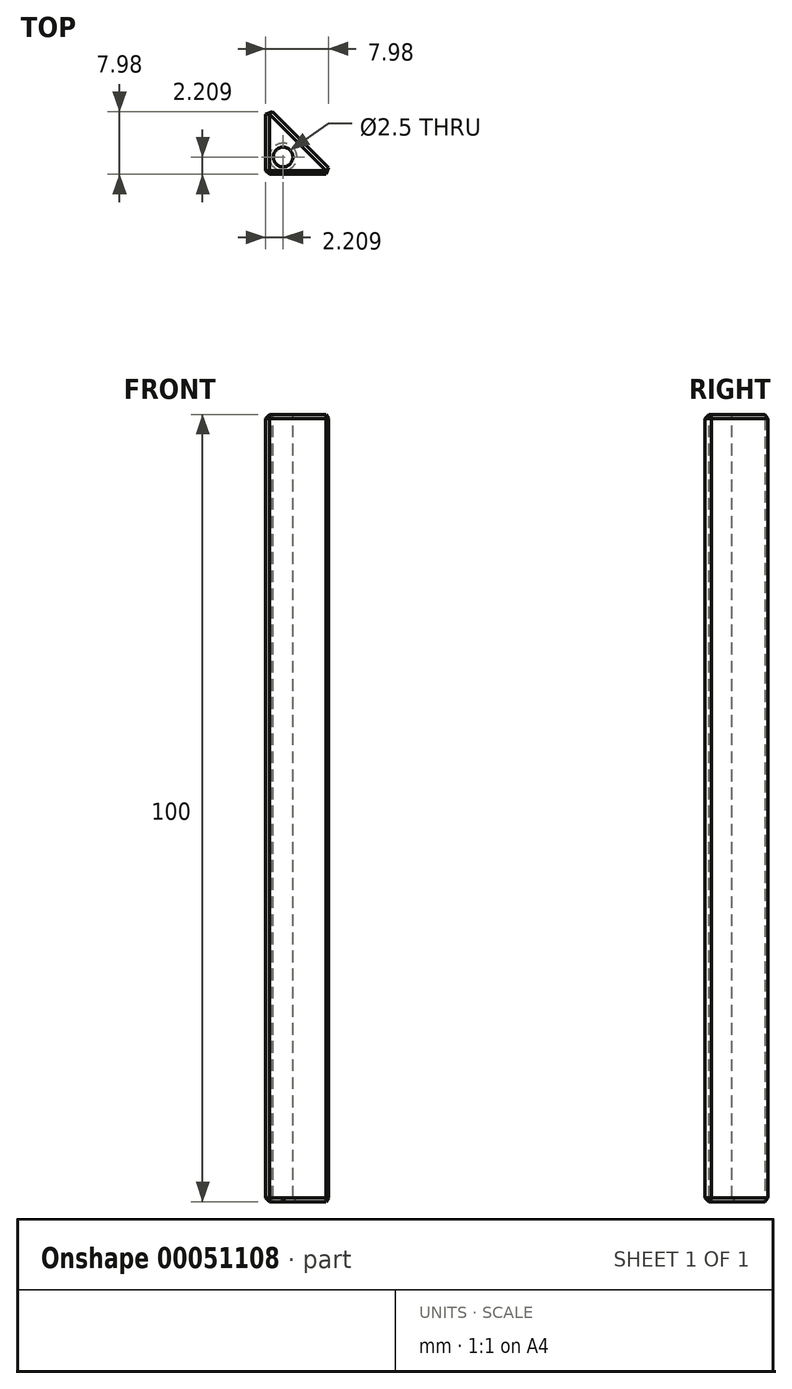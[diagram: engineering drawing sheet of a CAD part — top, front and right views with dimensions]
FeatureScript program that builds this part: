
annotation { "Feature Type Name" : "Feature", "Feature Type Description" : "" }
export const myFeature = defineFeature(function(context is Context, id is Id, definition is map)
    precondition{}
    {
        {
            var Q0;
            Q0=qCreatedBy(makeId("Top.planeOp"),FACE);
            var sketch = newSketch(context, id + "F0", { "sketchPlane" : qUnion([Q0])});
            skLineSegment(sketch, "E0.bottom", {"start": v(0, 0) * mm, "end": v(8.84, 0) * mm});
            skLineSegment(sketch, "E0.top", {"start": v(0, 8.84) * mm, "end": v(8.84, 8.84) * mm});
            skLineSegment(sketch, "E0.left", {"start": v(0, 0) * mm, "end": v(0, 8.84) * mm});
            skLineSegment(sketch, "E0.right", {"start": v(8.84, 0) * mm, "end": v(8.84, 8.84) * mm});
            skSolve(sketch);
        }
        {
            var Q0;
            Q0 = qSketchRegion(id + "F0", true);
            extrude(context, id + "F1", {"entities" : qUnion([Q0]), "depth" : 100 * mm});
        }
        {
            var Q0;
            Q0=makeQuery(id+"F1.opExtrude","CAP_FACE",FACE,{"disambiguationData":[OSD([sQuery(id+"F0.wireOp",EDGE,"E0.bottom"),sQuery(id+"F0.wireOp",EDGE,"E0.top"),sQuery(id+"F0.wireOp",EDGE,"E0.left"),sQuery(id+"F0.wireOp",EDGE,"E0.right")])],"isStart":false});
            var sketch = newSketch(context, id + "F2", { "sketchPlane" : qUnion([Q0])});
            skLineSegment(sketch, "E1", {"start": v(0, 8.84) * mm, "end": v(8.84, 8.84) * mm});
            skLineSegment(sketch, "E2", {"start": v(8.84, 8.84) * mm, "end": v(8.84, 0) * mm});
            skLineSegment(sketch, "E3", {"start": v(8.84, 0) * mm, "end": v(0, 8.84) * mm});
            skSolve(sketch);
        }
        {
            var Q0;
            Q0=makeQuery(id+"F2.imprint","IMPRINT",FACE,{"disambiguationData":[TD([[makeQuery(id+"F2.imprint","IMPRINT",EDGE,{"derivedFrom":sQuery(id+"F2.wireOp",EDGE,"E1")}),-1.0]])]});
            extrude(context, id + "F3", {"entities" : qUnion([Q0]), "operationType" : NewBodyOperationType.REMOVE, "oppositeDirection" : true, "depth" : 100 * mm});
        }
        {
            var Q0;
            Q0=makeQuery(id+"F1.opExtrude","CAP_FACE",FACE,{"disambiguationData":[OSD([sQuery(id+"F0.wireOp",EDGE,"E0.bottom"),sQuery(id+"F0.wireOp",EDGE,"E0.top"),sQuery(id+"F0.wireOp",EDGE,"E0.left"),sQuery(id+"F0.wireOp",EDGE,"E0.right")])],"isStart":false});
            var sketch = newSketch(context, id + "F4", { "sketchPlane" : qUnion([Q0])});
            skCircle(sketch, "E4", {"center": v(2.2, 2.2) * mm, "radius": 1.25 * mm});
            skSolve(sketch);
        }
        {
            var Q0;
            Q0 = qSketchRegion(id + "F4", true);
            extrude(context, id + "F5", {"entities" : qUnion([Q0]), "operationType" : NewBodyOperationType.REMOVE, "oppositeDirection" : true, "depth" : 100 * mm});
        }
        {
            var Q0;
            Q0=makeQuery(id+"F3.boolean.opBoolean","COPY",FACE,{"derivedFrom":makeQuery(id+"F3.opExtrude","SWEPT_FACE",FACE,{"disambiguationData":[OSD([sQuery(id+"F2.wireOp",EDGE,"E3")])]})});
            var Q1;
            Q1=makeQuery(id+"F1.opExtrude","CAP_FACE",FACE,{"disambiguationData":[OSD([sQuery(id+"F0.wireOp",EDGE,"E0.bottom"),sQuery(id+"F0.wireOp",EDGE,"E0.top"),sQuery(id+"F0.wireOp",EDGE,"E0.left"),sQuery(id+"F0.wireOp",EDGE,"E0.right")])],"isStart":true});
            var Q2;
            Q2=makeQuery(id+"F1.opExtrude","SWEPT_FACE",FACE,{"disambiguationData":[OSD([sQuery(id+"F0.wireOp",EDGE,"E0.left")])]});
            var Q3;
            Q3=makeQuery(id+"F1.opExtrude","SWEPT_FACE",FACE,{"disambiguationData":[OSD([sQuery(id+"F0.wireOp",EDGE,"E0.bottom")])]});
            chamfer(context, id + "F6", {"entities" : qUnion([Q0, Q1, Q2, Q3]), "width" : 0.5 * mm, "tangentPropagation" : true});
        }
    });
